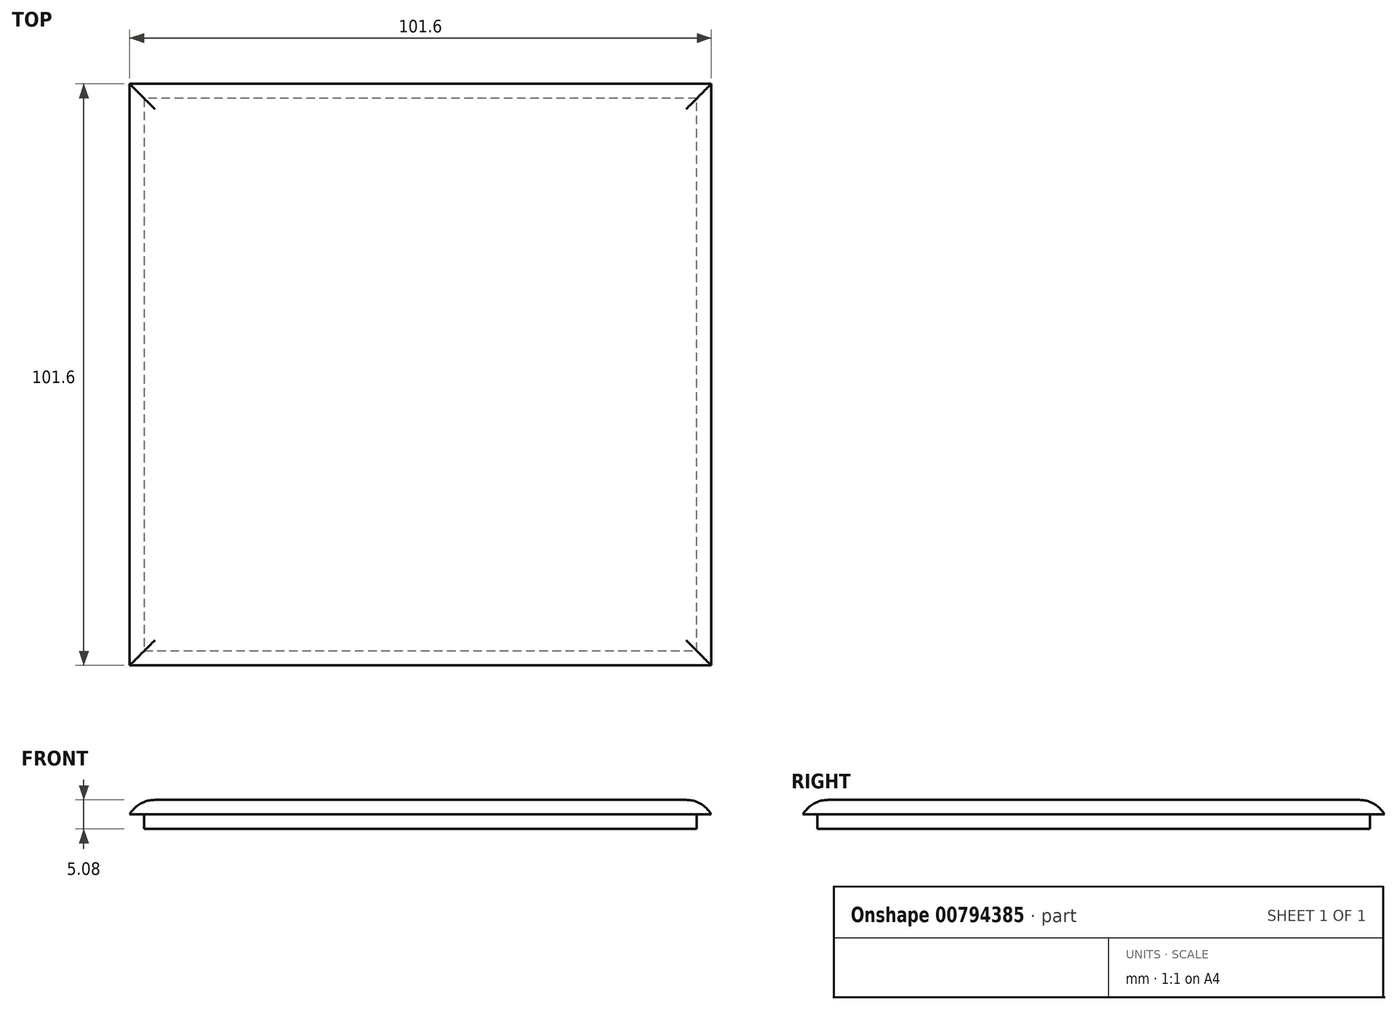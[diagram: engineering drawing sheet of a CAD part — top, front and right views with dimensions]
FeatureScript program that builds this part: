
annotation { "Feature Type Name" : "Feature", "Feature Type Description" : "" }
export const myFeature = defineFeature(function(context is Context, id is Id, definition is map)
    precondition{}
    {
        {
            var Q0;
            Q0=qCreatedBy(makeId("Top.planeOp"),FACE);
            cPlane(context, id + "F0", {"entities" : qUnion([Q0]), "cplaneType" : CPlaneType.OFFSET, "offset" : 101.6 * mm, "width" : 152.4 * mm, "height" : 152.4 * mm});
        }
        {
            var Q0;
            Q0=qCreatedBy(id+"F0.planeOp",FACE);
            var sketch = newSketch(context, id + "F1", { "sketchPlane" : qUnion([Q0])});
            skLineSegment(sketch, "E0.0", {"start": v(-181.27, -12.92) * mm, "end": v(-181.27, -114.52) * mm});
            skLineSegment(sketch, "E1.0", {"start": v(-79.67, -12.92) * mm, "end": v(-181.27, -12.92) * mm});
            skLineSegment(sketch, "E2.0", {"start": v(-79.67, -114.52) * mm, "end": v(-79.67, -12.92) * mm});
            skLineSegment(sketch, "E3.0", {"start": v(-181.27, -114.52) * mm, "end": v(-79.67, -114.52) * mm});
            skLineSegment(sketch, "E4.0", {"start": v(-178.73, -15.46) * mm, "end": v(-178.73, -111.98) * mm});
            skLineSegment(sketch, "E5.0", {"start": v(-82.2, -15.46) * mm, "end": v(-178.73, -15.46) * mm});
            skLineSegment(sketch, "E6.0", {"start": v(-82.2, -111.98) * mm, "end": v(-82.2, -15.46) * mm});
            skLineSegment(sketch, "E7.0", {"start": v(-178.73, -111.98) * mm, "end": v(-82.2, -111.98) * mm});
            skSolve(sketch);
        }
        {
            var Q0;
            Q0 = qSketchRegion(id + "F1", true);
            var Q1;
            Q1=makeQuery(id+"F1.imprint","IMPRINT",FACE,{"disambiguationData":[TD([[makeQuery(id+"F1.imprint","IMPRINT",EDGE,{"derivedFrom":sQuery(id+"F1.wireOp",EDGE,"E4.0")}),1.0]])]});
            extrude(context, id + "F2", {"entities" : qUnion([Q0, Q1]), "depth" : 2.54 * mm, "offsetDistance" : 25.4 * mm});
        }
        {
            var Q0;
            Q0=makeQuery(id+"F2.opExtrude","CAP_EDGE",EDGE,{"disambiguationData":[OSD([sQuery(id+"F1.wireOp",EDGE,"E3.0")])],"isStart":false});
            var Q1;
            Q1=makeQuery(id+"F2.opExtrude","CAP_EDGE",EDGE,{"disambiguationData":[OSD([sQuery(id+"F1.wireOp",EDGE,"E2.0")])],"isStart":false});
            var Q2;
            Q2=makeQuery(id+"F2.opExtrude","CAP_EDGE",EDGE,{"disambiguationData":[OSD([sQuery(id+"F1.wireOp",EDGE,"E1.0")])],"isStart":false});
            var Q3;
            Q3=makeQuery(id+"F2.opExtrude","CAP_EDGE",EDGE,{"disambiguationData":[OSD([sQuery(id+"F1.wireOp",EDGE,"E0.0")])],"isStart":false});
            fillet(context, id + "F3", {"entities" : qUnion([Q0, Q1, Q2, Q3]), "radius" : 5.08 * mm, "tangentPropagation" : true, "allowEdgeOverflow" : false});
        }
        {
            var Q0;
            Q0=makeQuery(id+"F1.imprint","IMPRINT",FACE,{"disambiguationData":[TD([[makeQuery(id+"F1.imprint","IMPRINT",EDGE,{"derivedFrom":sQuery(id+"F1.wireOp",EDGE,"E4.0")}),1.0]])]});
            extrude(context, id + "F4", {"entities" : qUnion([Q0]), "operationType" : NewBodyOperationType.ADD, "oppositeDirection" : true, "depth" : 2.54 * mm, "offsetDistance" : 25.4 * mm});
        }
    });
